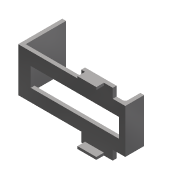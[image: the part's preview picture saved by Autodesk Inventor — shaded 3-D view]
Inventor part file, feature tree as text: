
AUTODESK INVENTOR PART (.ipt)
format: ipt  version: 2018 (Build 220112000, 112)  size: 179,200 bytes
history: native  units: mm
features: extrude x4, sketch x4, fillet x2
ambient origin geometry x8: Origin, YZ Plane, XZ Plane, XY Plane, X Axis, Y Axis, Z Axis, Center Point
bodies: Volumenkörper1 (feature_tree)
feature tree (10):
  extrude  "Extrusion1"  Depth=25.0mm
  extrude  "Extrusion2"  Depth=35.0mm
  fillet  "Rundung1"  Radius=10.0mm
  extrude  "Extrusion3"  Depth=70.0mm
  extrude  "Extrusion4"  Depth=3.0mm TaperAngle=0.0deg
  fillet  "Rundung2"  Radius=3.0mm
  sketch  "Skizze1"  dims[d0=50.0mm d1=25.0mm]
  sketch  "Skizze2"  dims[d2=7.5mm d4=35.0mm d5=10.0mm]
  sketch  "Skizze3"  dims[d6=15.0mm d8=70.0mm]
  sketch  "Skizze4"  dims[d9=65.0mm d10=3.0mm d11=0.0mm d12=3.0mm d13=12.0mm d14=3.0mm d15=0.0mm d16=2.0mm d17=2.0mm d18=2.0mm d19=46.0mm d20=15.0mm d21=15.0mm d22=0.0mm d23=7.0mm d24=6.0mm d25=0.0mm d26=50.0mm d27=35.0mm d28=7.5mm d29=35.0mm d30=3.0mm d31=0.0mm d32=7.0mm]
